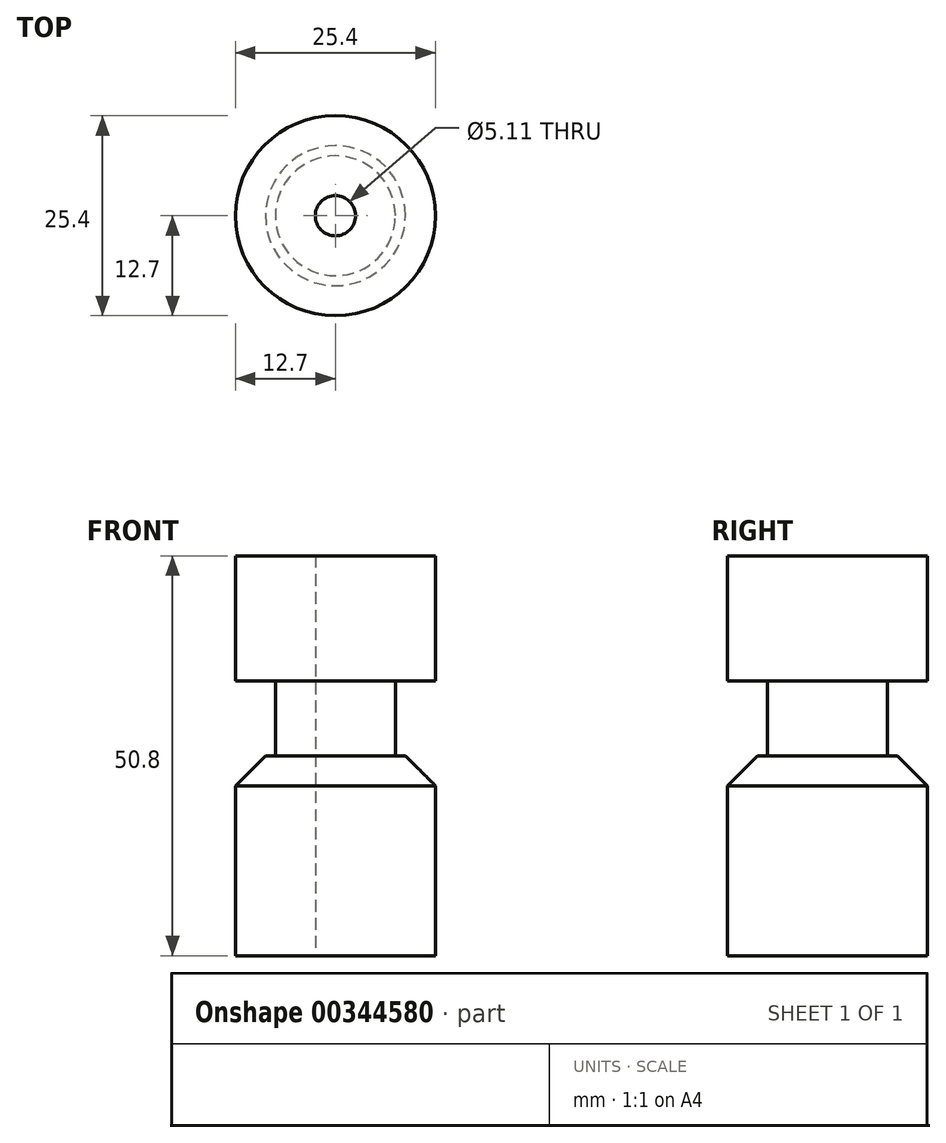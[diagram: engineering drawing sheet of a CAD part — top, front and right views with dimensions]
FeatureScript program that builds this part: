
annotation { "Feature Type Name" : "Feature", "Feature Type Description" : "" }
export const myFeature = defineFeature(function(context is Context, id is Id, definition is map)
    precondition{}
    {
        {
            var Q0;
            Q0=qCreatedBy(makeId("Top.planeOp"),FACE);
            var sketch = newSketch(context, id + "F0", { "sketchPlane" : qUnion([Q0])});
            skCircle(sketch, "E0", {"center": v(0, 0) * mm, "radius": 12.7 * mm});
            skSolve(sketch);
        }
        {
            var Q0;
            Q0 = qSketchRegion(id + "F0", true);
            extrude(context, id + "F1", {"entities" : qUnion([Q0]), "depth" : 50.8 * mm});
        }
        {
            var Q0;
            Q0=qCreatedBy(makeId("Right.planeOp"),FACE);
            var sketch = newSketch(context, id + "F2", { "sketchPlane" : qUnion([Q0])});
            skLineSegment(sketch, "E1.bottom", {"start": v(-7.62, 34.93) * mm, "end": v(-12.7, 34.93) * mm});
            skLineSegment(sketch, "E1.top", {"start": v(-7.62, 25.4) * mm, "end": v(-12.7, 25.4) * mm});
            skLineSegment(sketch, "E1.left", {"start": v(-7.62, 34.92) * mm, "end": v(-7.62, 25.4) * mm});
            skLineSegment(sketch, "E1.right", {"start": v(-12.7, 34.92) * mm, "end": v(-12.7, 25.4) * mm});
            skLineSegment(sketch, "E2", {"start": v(0, 0) * mm, "end": v(0, 69.4) * mm});
            skSolve(sketch);
        }
        {
            var Q0;
            Q0 = qSketchRegion(id + "F2", true);
            var Q1;
            Q1=sQuery(id+"F2.wireOp",EDGE,"E2");
            revolve(context, id + "F3", {"operationType" : NewBodyOperationType.REMOVE, "entities" : qUnion([Q0]), "axis" : qUnion([Q1]), "revolveType" : RevolveType.FULL, "oppositeDirection" : true});
        }
        {
            var Q0;
            Q0=makeQuery(id+"F3.boolean.opBoolean","COPY",EDGE,{"derivedFrom":makeQuery(id+"F3.opRevolve","SWEPT_EDGE",EDGE,{"disambiguationData":[OSD([sQuery(id+"F2.wireOp",EDGE,"E1.bottom"),sQuery(id+"F2.wireOp",EDGE,"E1.right")])]})});
            var Q1;
            Q1=makeQuery(id+"F3.boolean.opBoolean","COPY",EDGE,{"derivedFrom":makeQuery(id+"F3.opRevolve","SWEPT_EDGE",EDGE,{"disambiguationData":[OSD([sQuery(id+"F2.wireOp",EDGE,"E1.top"),sQuery(id+"F2.wireOp",EDGE,"E1.right")])]})});
            chamfer(context, id + "F4", {"entities" : qUnion([Q0, Q1]), "width" : 3.8 * mm, "tangentPropagation" : true});
        }
        {
            var Q0;
            Q0=qCreatedBy(makeId("Top.planeOp"),FACE);
            var sketch = newSketch(context, id + "F5", { "sketchPlane" : qUnion([Q0])});
            skPoint(sketch, "E3", {"position": v(0, 0) * mm});
            skSolve(sketch);
        }
        {
            var Q0;
            Q0=sQuery(id+"F5.wireOp",VERTEX,"E3");
            var Q1;
            Q1=makeQuery(id+"F1.opExtrude","SWEPT_BODY",BODY,{"disambiguationData":[OSD([sQuery(id+"F0.wireOp",EDGE,"E0")])]});
            hole(context, id + "F6", {"style" : HoleStyle.SIMPLE, "endStyle" : HoleEndStyle.THROUGH, "oppositeDirection" : true, "standardTappedOrClearance" : lookupTablePath({ "standard" : "ANSI", "engagement" : "75%", "pitch" : "20 tpi", "size" : "1/4", "type" : "Tapped" }), "standardBlindInLast" : lookupTablePath({ "standard" : "ANSI", "engagement" : "75%", "pitch" : "20 tpi", "size" : "1/4", "type" : "Tapped" }), "holeDiameter" : 5.1 * mm, "showTappedDepth" : true, "isTappedThrough" : true, "tappedDepth" : 12.7 * mm, "tapClearance" : 3, "locations" : qUnion([Q0]), "scope" : qUnion([Q1]), "majorDiameter" : 6.35 * mm});
        }
    });
